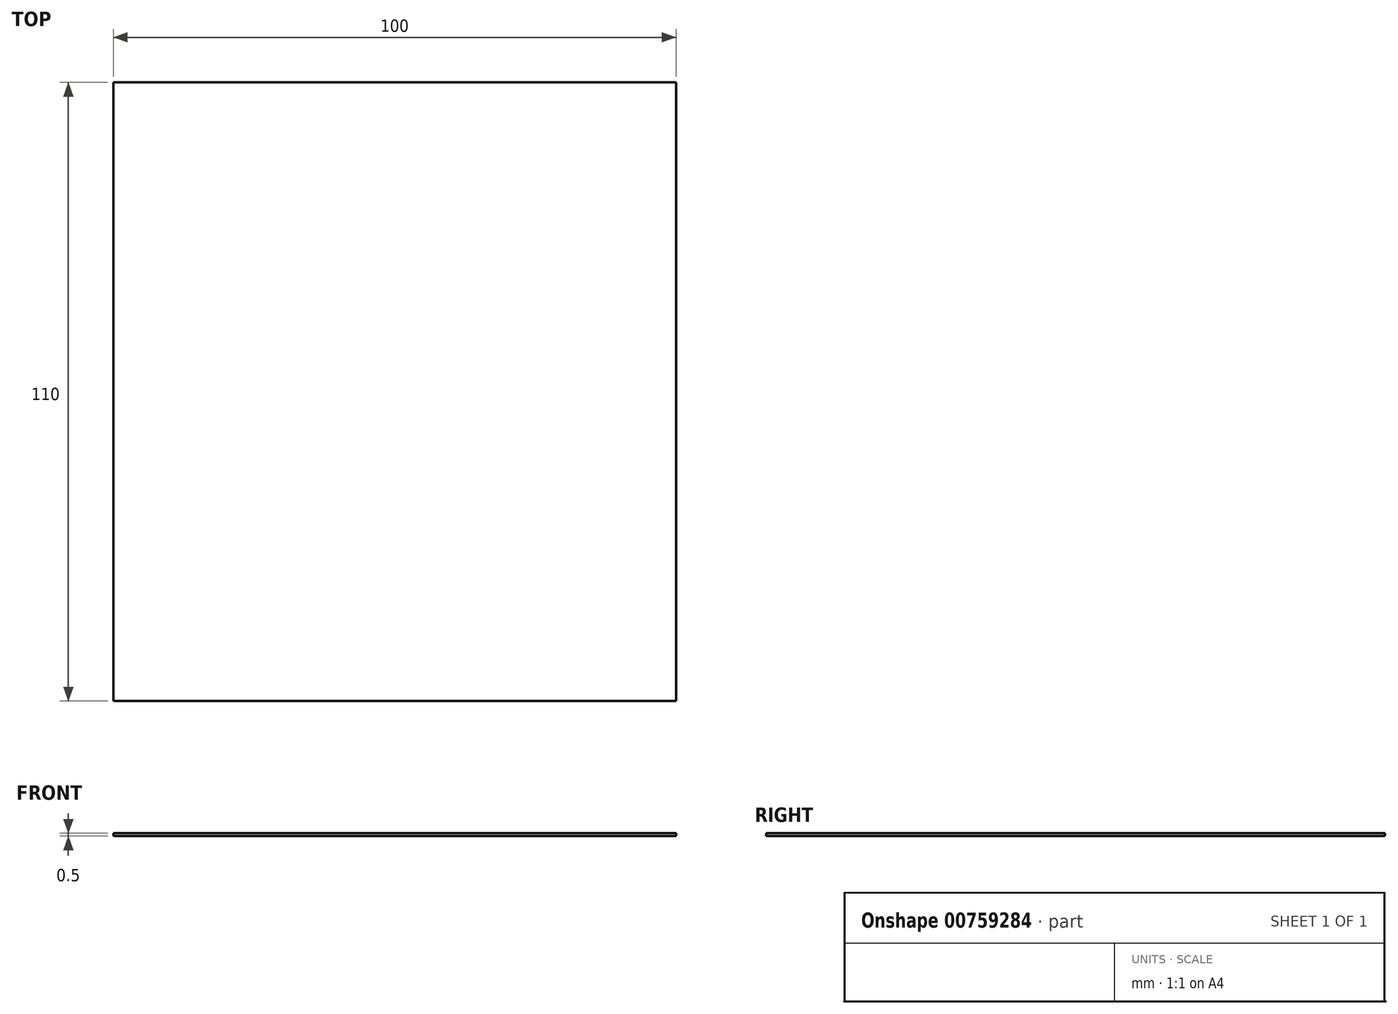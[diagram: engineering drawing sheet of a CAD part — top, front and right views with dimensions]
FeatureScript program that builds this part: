
annotation { "Feature Type Name" : "Feature", "Feature Type Description" : "" }
export const myFeature = defineFeature(function(context is Context, id is Id, definition is map)
    precondition{}
    {
        {
            var Q0;
            Q0=qCreatedBy(makeId("Top.planeOp"),FACE);
            var sketch = newSketch(context, id + "F0", { "sketchPlane" : qUnion([Q0])});
            skLineSegment(sketch, "E0.bottom", {"start": v(50, -55) * mm, "end": v(-50, -55) * mm});
            skLineSegment(sketch, "E0.top", {"start": v(50, 55) * mm, "end": v(-50, 55) * mm});
            skLineSegment(sketch, "E0.left", {"start": v(50, -55) * mm, "end": v(50, 55) * mm});
            skLineSegment(sketch, "E0.right", {"start": v(-50, -55) * mm, "end": v(-50, 55) * mm});
            skPoint(sketch, "E0.middle", {"position": v(0, 0) * mm});
            skSolve(sketch);
        }
        {
            var Q0;
            Q0=makeQuery(id+"F0.imprint","IMPRINT",FACE,{"disambiguationData":[TD([[makeQuery(id+"F0.imprint","IMPRINT",EDGE,{"derivedFrom":sQuery(id+"F0.wireOp",EDGE,"E0.bottom")}),-1.0]])]});
            extrude(context, id + "F1", {"entities" : qUnion([Q0]), "depth" : 0.5 * mm, "offsetDistance" : 25 * mm});
        }
    });
